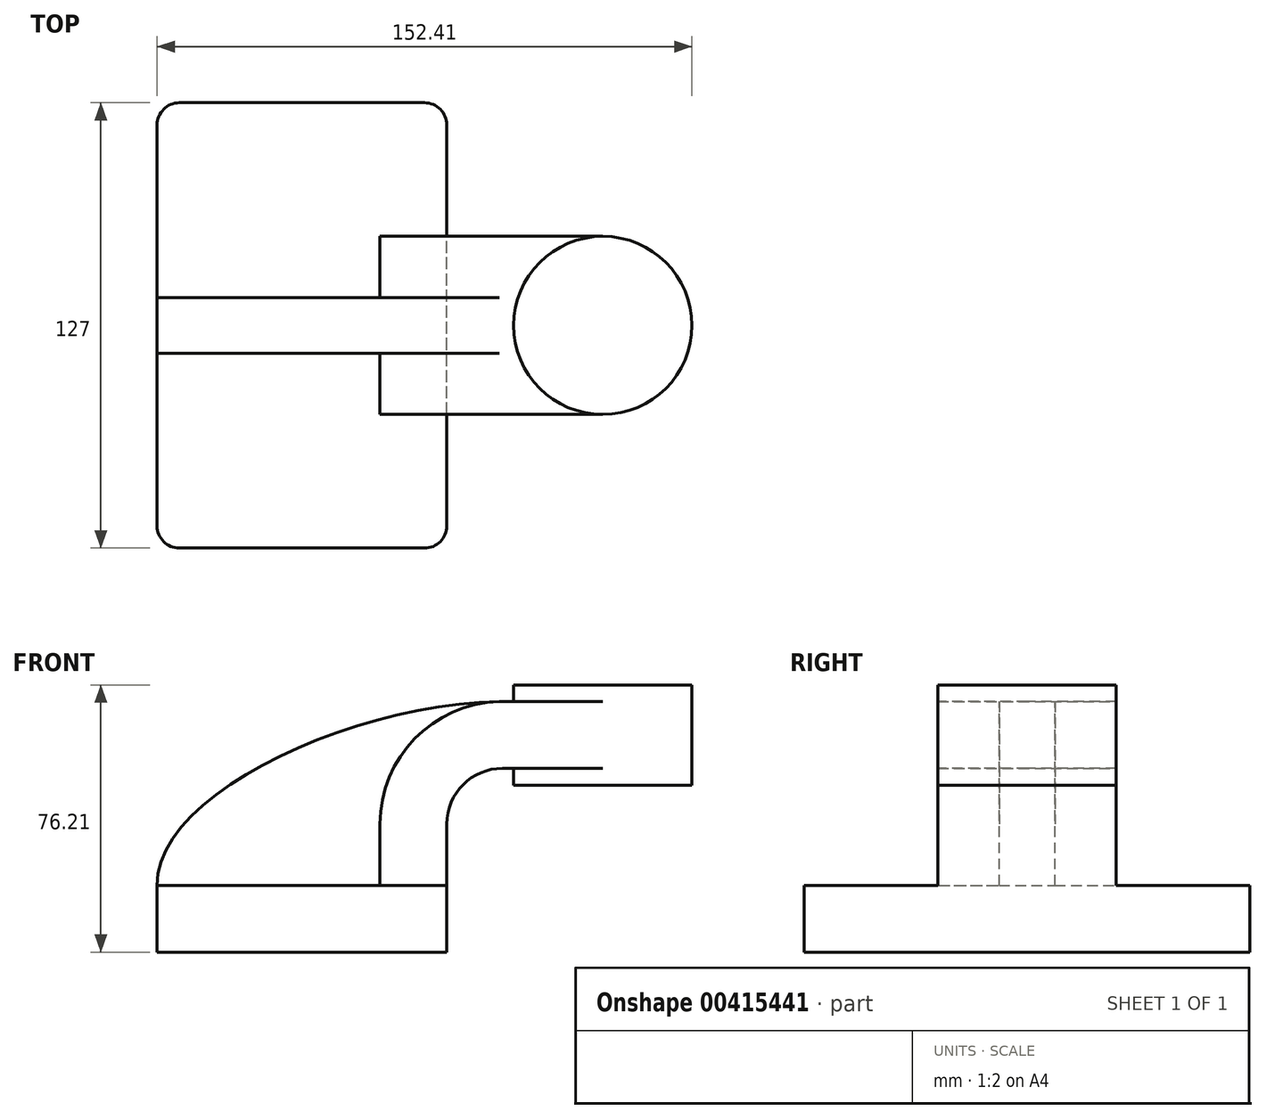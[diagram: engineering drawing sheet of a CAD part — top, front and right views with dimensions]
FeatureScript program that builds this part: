
annotation { "Feature Type Name" : "Feature", "Feature Type Description" : "" }
export const myFeature = defineFeature(function(context is Context, id is Id, definition is map)
    precondition{}
    {
        {
            var Q0;
            Q0=qCreatedBy(makeId("Front.planeOp"),FACE);
            var sketch = newSketch(context, id + "F0", { "sketchPlane" : qUnion([Q0])});
            skLineSegment(sketch, "E0.bottom", {"start": v(-41.28, -9.53) * mm, "end": v(41.28, -9.53) * mm});
            skLineSegment(sketch, "E0.top", {"start": v(-41.28, 9.53) * mm, "end": v(41.28, 9.53) * mm});
            skLineSegment(sketch, "E0.left", {"start": v(-41.28, -9.53) * mm, "end": v(-41.28, 9.53) * mm});
            skLineSegment(sketch, "E0.right", {"start": v(41.28, -9.53) * mm, "end": v(41.28, 9.52) * mm});
            skPoint(sketch, "E0.middle", {"position": v(0, 0) * mm});
            skLineSegment(sketch, "E1.bottom", {"start": v(111.13, 38.1) * mm, "end": v(60.32, 38.1) * mm});
            skLineSegment(sketch, "E1.top", {"start": v(111.13, 66.67) * mm, "end": v(60.32, 66.67) * mm});
            skLineSegment(sketch, "E1.left", {"start": v(111.12, 38.1) * mm, "end": v(111.12, 66.67) * mm});
            skLineSegment(sketch, "E1.right", {"start": v(60.32, 38.1) * mm, "end": v(60.32, 66.67) * mm});
            skPoint(sketch, "E1.middle", {"position": v(85.72, 52.39) * mm});
            skLineSegment(sketch, "E2", {"start": v(41.28, 9.53) * mm, "end": v(41.28, 27) * mm});
            skArc(sketch, "E3", {"start": v(41.28, 27) * mm, "mid": v(45.92, 38.23) * mm, "end": v(57.15, 42.88) * mm});
            skLineSegment(sketch, "E4", {"start": v(57.15, 42.88) * mm, "end": v(85.72, 42.88) * mm});
            skPoint(sketch, "E5", {"position": v(85.72, 38.1) * mm});
            skLineSegment(sketch, "E6.0", {"start": v(57.15, 61.93) * mm, "end": v(85.72, 61.93) * mm});
            skArc(sketch, "E6.1", {"start": v(22.23, 27) * mm, "mid": v(32.45, 51.7) * mm, "end": v(57.15, 61.93) * mm});
            skLineSegment(sketch, "E6.2", {"start": v(22.23, 9.53) * mm, "end": v(22.23, 27) * mm});
            skLineSegment(sketch, "E7", {"start": v(85.72, 38.1) * mm, "end": v(85.72, 66.67) * mm});
            skFitSpline(sketch, "E8", {"points": [v(-41.28, 9.53) * mm, v(57.15, 61.93) * mm], "startDerivative": vector(-1.5, 77.64) * mm, "endDerivative": vector(128.77, 1.23) * mm});
            skSolve(sketch);
        }
        {
            var Q0;
            Q0=makeQuery(id+"F0.imprint","IMPRINT",FACE,{"disambiguationData":[TD([[makeQuery(id+"F0.imprint","IMPRINT",EDGE,{"derivedFrom":sQuery(id+"F0.wireOp",EDGE,"E0.bottom")}),1.0]])]});
            extrude(context, id + "F1", {"entities" : qUnion([Q0]), "endBound" : BoundingType.SYMMETRIC, "depth" : 127 * mm, "offsetDistance" : 25.4 * mm});
        }
        {
            var Q0;
            {var subQ1=sQuery(id+"F0.wireOp",EDGE,"E2");Q0=makeQuery(id+"F0.imprint","IMPRINT",FACE,{"disambiguationData":[TD([[makeQuery(id+"F0.imprint","IMPRINT",EDGE,{"derivedFrom":subQ1}),1.0]])]});}
            var Q1;
            {var subQ0=sQuery(id+"F0.wireOp",EDGE,"E4");var subQ1=sQuery(id+"F0.wireOp",EDGE,"E1.right");var subQ2=makeQuery(id+"F0.imprint","INTERSECT",VERTEX,{"derivedFrom":[subQ1,subQ0]});Q1=makeQuery(id+"F0.imprint","IMPRINT",FACE,{"disambiguationData":[TD([[makeQuery(id+"F0.imprint","IMPRINT",EDGE,{"disambiguationData":[TD([[subQ2,-1.0]])],"derivedFrom":subQ1}),-1.0]])]});}
            extrude(context, id + "F2", {"entities" : qUnion([Q0, Q1]), "operationType" : NewBodyOperationType.ADD, "endBound" : BoundingType.SYMMETRIC, "depth" : 50.8 * mm, "offsetDistance" : 25.4 * mm});
        }
        {
            var Q0;
            {var subQ3=sQuery(id+"F0.wireOp",EDGE,"E6.2");Q0=makeQuery(id+"F0.imprint","IMPRINT",FACE,{"disambiguationData":[TD([[makeQuery(id+"F0.imprint","IMPRINT",EDGE,{"derivedFrom":subQ3}),1.0]])]});}
            extrude(context, id + "F3", {"entities" : qUnion([Q0]), "operationType" : NewBodyOperationType.ADD, "endBound" : BoundingType.SYMMETRIC, "depth" : 15.88 * mm, "offsetDistance" : 25.4 * mm});
        }
        {
            var Q0;
            {var subQ0=sQuery(id+"F0.wireOp",EDGE,"E1.left");Q0=makeQuery(id+"F0.imprint","IMPRINT",FACE,{"disambiguationData":[TD([[makeQuery(id+"F0.imprint","IMPRINT",EDGE,{"derivedFrom":subQ0}),1.0]])]});}
            var Q1;
            Q1=sQuery(id+"F0.wireOp",EDGE,"E7");
            revolve(context, id + "F4", {"operationType" : NewBodyOperationType.ADD, "entities" : qUnion([Q0]), "axis" : qUnion([Q1]), "revolveType" : RevolveType.FULL});
        }
        {
            var Q0;
            Q0=makeQuery(id+"F1.opExtrude","CAP_EDGE",EDGE,{"disambiguationData":[OSD([sQuery(id+"F0.wireOp",EDGE,"E0.right")])],"isStart":false});
            var Q1;
            Q1=makeQuery(id+"F1.opExtrude","CAP_EDGE",EDGE,{"disambiguationData":[OSD([sQuery(id+"F0.wireOp",EDGE,"E0.left")])],"isStart":false});
            var Q2;
            Q2=makeQuery(id+"F1.opExtrude","CAP_EDGE",EDGE,{"disambiguationData":[OSD([sQuery(id+"F0.wireOp",EDGE,"E0.right")])],"isStart":true});
            var Q3;
            Q3=makeQuery(id+"F1.opExtrude","CAP_EDGE",EDGE,{"disambiguationData":[OSD([sQuery(id+"F0.wireOp",EDGE,"E0.left")])],"isStart":true});
            fillet(context, id + "F5", {"entities" : qUnion([Q0, Q1, Q2, Q3]), "radius" : 6.35 * mm, "tangentPropagation" : true, "allowEdgeOverflow" : false});
        }
    });
